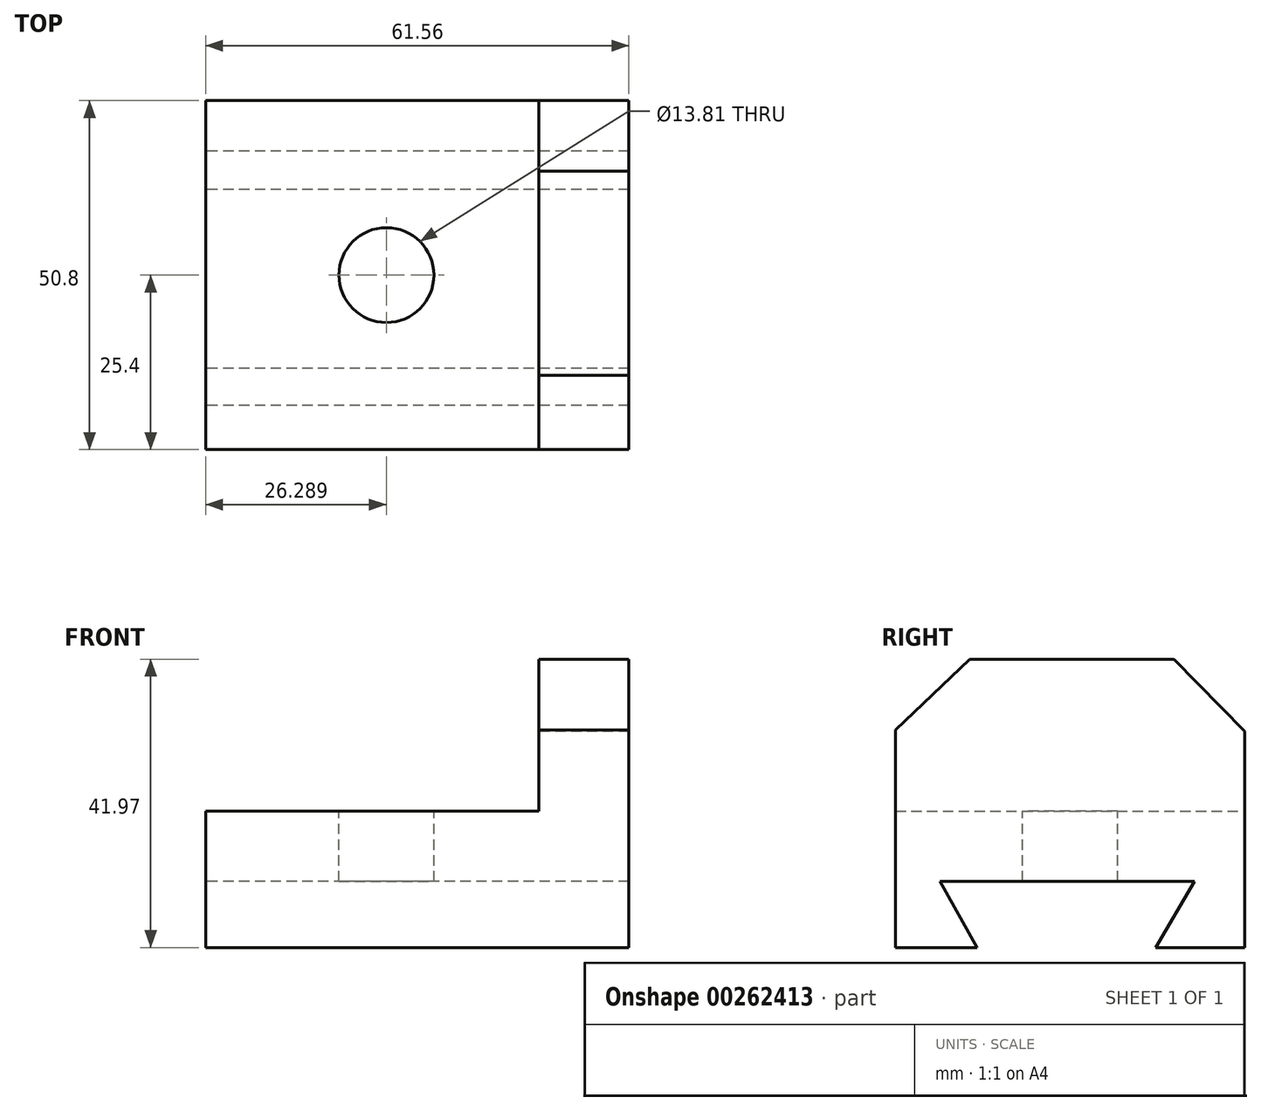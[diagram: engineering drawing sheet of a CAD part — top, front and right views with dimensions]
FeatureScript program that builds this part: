
annotation { "Feature Type Name" : "Feature", "Feature Type Description" : "" }
export const myFeature = defineFeature(function(context is Context, id is Id, definition is map)
    precondition{}
    {
        {
            var Q0;
            Q0=qCreatedBy(makeId("Front.planeOp"),FACE);
            var sketch = newSketch(context, id + "F0", { "sketchPlane" : qUnion([Q0])});
            skLineSegment(sketch, "E0", {"start": v(-32.41, 15.3) * mm, "end": v(-32.41, -4.52) * mm});
            skLineSegment(sketch, "E1", {"start": v(-32.41, 15.3) * mm, "end": v(16.03, 15.3) * mm});
            skLineSegment(sketch, "E2", {"start": v(16.03, 15.3) * mm, "end": v(16.03, 37.45) * mm});
            skLineSegment(sketch, "E3", {"start": v(16.03, 37.45) * mm, "end": v(29.15, 37.45) * mm});
            skLineSegment(sketch, "E4", {"start": v(29.15, 37.45) * mm, "end": v(29.15, -4.52) * mm});
            skLineSegment(sketch, "E5", {"start": v(29.15, -4.52) * mm, "end": v(-32.41, -4.52) * mm});
            skSolve(sketch);
        }
        {
            var Q0;
            Q0 = qSketchRegion(id + "F0", true);
            extrude(context, id + "F1", {"entities" : qUnion([Q0]), "depth" : 25.4 * mm, "hasSecondDirection" : true, "secondDirectionOppositeDirection" : true, "secondDirectionDepth" : 25.4 * mm});
        }
        {
            var Q0;
            Q0=makeQuery(id+"F1.opExtrude","SWEPT_FACE",FACE,{"disambiguationData":[OSD([sQuery(id+"F0.wireOp",EDGE,"E2")])]});
            var sketch = newSketch(context, id + "F2", { "sketchPlane" : qUnion([Q0])});
            skLineSegment(sketch, "E6", {"start": v(-14.28, 38.33) * mm, "end": v(-26.82, 25.5) * mm});
            skLineSegment(sketch, "E7", {"start": v(27.1, 25.5) * mm, "end": v(13.7, 38.33) * mm});
            skSolve(sketch);
        }
        {
            var Q0;
            {var subQ0=sQuery(id+"F2.wireOp",EDGE,"E6");var subQ1=sQuery(id+"F0.wireOp",EDGE,"E2");var subQ4=makeQuery(id+"F1.opExtrude","CAP_EDGE",EDGE,{"disambiguationData":[OSD([subQ1])],"isStart":true});var subQ5=makeQuery(id+"F2.imprint","INTERSECT",VERTEX,{"derivedFrom":[subQ4,subQ0]});Q0=makeQuery(id+"F2.imprint","IMPRINT",FACE,{"disambiguationData":[TD([[makeQuery(id+"F2.imprint","IMPRINT",EDGE,{"disambiguationData":[TD([[subQ5,1.0]])],"derivedFrom":subQ0}),-1.0]])]});}
            var Q1;
            {var subQ0=sQuery(id+"F2.wireOp",EDGE,"E7");var subQ1=sQuery(id+"F0.wireOp",EDGE,"E2");var subQ4=makeQuery(id+"F1.opExtrude","CAP_EDGE",EDGE,{"disambiguationData":[OSD([subQ1])],"isStart":false});var subQ5=makeQuery(id+"F2.imprint","INTERSECT",VERTEX,{"derivedFrom":[subQ4,subQ0]});Q1=makeQuery(id+"F2.imprint","IMPRINT",FACE,{"disambiguationData":[TD([[makeQuery(id+"F2.imprint","IMPRINT",EDGE,{"disambiguationData":[TD([[subQ5,-1.0]])],"derivedFrom":subQ0}),-1.0]])]});}
            extrude(context, id + "F3", {"entities" : qUnion([Q0, Q1]), "operationType" : NewBodyOperationType.REMOVE, "oppositeDirection" : true, "depth" : 25.4 * mm});
        }
        {
            var Q0;
            Q0=makeQuery(id+"F1.opExtrude","SWEPT_FACE",FACE,{"disambiguationData":[OSD([sQuery(id+"F0.wireOp",EDGE,"E0")])]});
            var sketch = newSketch(context, id + "F4", { "sketchPlane" : qUnion([Q0])});
            skLineSegment(sketch, "E8", {"start": v(18.95, 5.1) * mm, "end": v(11.08, -8.9) * mm});
            skLineSegment(sketch, "E9", {"start": v(11.08, -8.9) * mm, "end": v(18.95, 5.1) * mm});
            skLineSegment(sketch, "E10", {"start": v(-18.07, 5.1) * mm, "end": v(-9.91, -8.9) * mm});
            skLineSegment(sketch, "E11", {"start": v(18.95, 5.1) * mm, "end": v(-18.07, 5.1) * mm});
            skSolve(sketch);
        }
        {
            var Q0;
            Q0 = qSketchRegion(id + "F4", true);
            var Q1;
            {var subQ0=sQuery(id+"F4.wireOp",EDGE,"E11");Q1=makeQuery(id+"F4.imprint","IMPRINT",FACE,{"disambiguationData":[TD([[makeQuery(id+"F4.imprint","IMPRINT",EDGE,{"derivedFrom":subQ0}),1.0]])]});}
            extrude(context, id + "F5", {"entities" : qUnion([Q0, Q1]), "operationType" : NewBodyOperationType.REMOVE, "oppositeDirection" : true, "depth" : 108.2 * mm});
        }
        {
            var Q0;
            Q0=makeQuery(id+"F1.opExtrude","SWEPT_FACE",FACE,{"disambiguationData":[OSD([sQuery(id+"F0.wireOp",EDGE,"E1")])]});
            var sketch = newSketch(context, id + "F6", { "sketchPlane" : qUnion([Q0])});
            skCircle(sketch, "E12", {"center": v(-6.12, 0) * mm, "radius": 6.9 * mm});
            skSolve(sketch);
        }
        {
            var Q0;
            Q0 = qSketchRegion(id + "F6", true);
            extrude(context, id + "F7", {"entities" : qUnion([Q0]), "operationType" : NewBodyOperationType.REMOVE, "oppositeDirection" : true, "depth" : 25.4 * mm});
        }
    });
